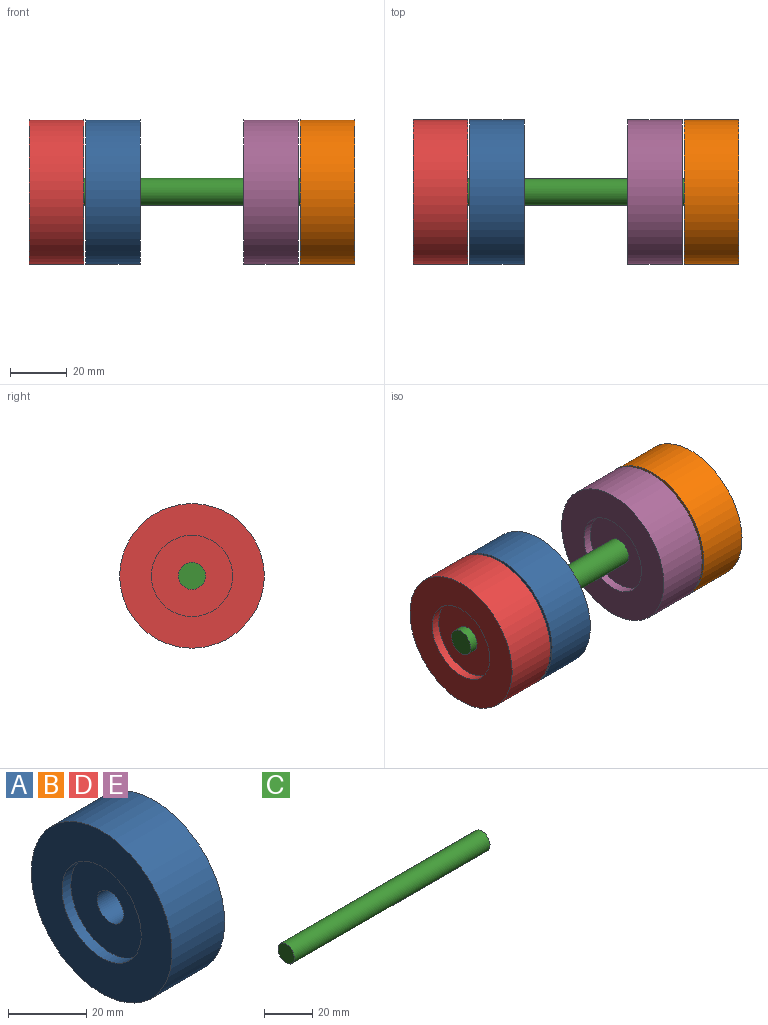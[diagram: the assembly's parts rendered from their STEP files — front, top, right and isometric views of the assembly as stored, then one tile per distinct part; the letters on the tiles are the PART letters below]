
ASSEMBLY  parts=5 mates=4
PART A: 8 faces, bbox 19.1x50.8x50.8 mm
  f0: cylinder r=25.4mm len=50.8mm, axis (1,0,0), area 3040.2mm2, adj f1,f7
  f1: plane 50.8x50.8mm, normal (1,0,0), area 1385.5mm2, adj f0,f2
  f2: cylinder r=14.29mm len=28.58mm, axis (1,0,0), area 285mm2, adj f1,f3
  f3: plane 28.58x28.58mm, normal (1,0,0), area 570mm2, adj f2,f4
  f4: cylinder r=4.76mm len=12.7mm, axis (1,0,0), area 380mm2, adj f3,f5
  f5: plane 28.58x28.58mm, normal (-1,0,0), area 570mm2, adj f4,f6
  f6: cylinder r=14.29mm len=28.58mm, axis (1,0,0), area 285mm2, adj f5,f7
  f7: plane 50.8x50.8mm, normal (-1,0,0), area 1385.5mm2, adj f0,f6
PART B: same geometry as A
PART C: 3 faces, bbox 114.3x9.5x9.5 mm
  f0: cylinder r=4.76mm len=114.3mm, axis (-1,0,0), area 3420.3mm2, adj f1,f2
  f1: plane 9.53x9.53mm, normal (1,0,0), area 71.3mm2, adj f0
  f2: plane 9.53x9.53mm, normal (-1,0,0), area 71.3mm2, adj f0
PART D: same geometry as A
PART E: same geometry as A
PLACE A t=(-75.41,-285.75,-15.87)mm
PLACE B t=(0,-285.75,-15.87)mm
PLACE C t=(0,-285.75,-15.87)mm fixed
PLACE D t=(-95.25,-285.75,-15.87)mm
PLACE E t=(-19.84,-285.75,-15.87)mm
MATE fastened D.f0 <-> A.f0  axis (1,0,0) through (-38.1,0,0)mm
MATE fastened D.f0 <-> C.f0  axis (-1,0,0) through (-57.15,0,0)mm
MATE fastened B.f0 <-> C.f0  axis (1,0,0) through (57.15,0,0)mm
MATE fastened E.f0 <-> B.f0  axis (1,0,0) through (37.31,0,0)mm
